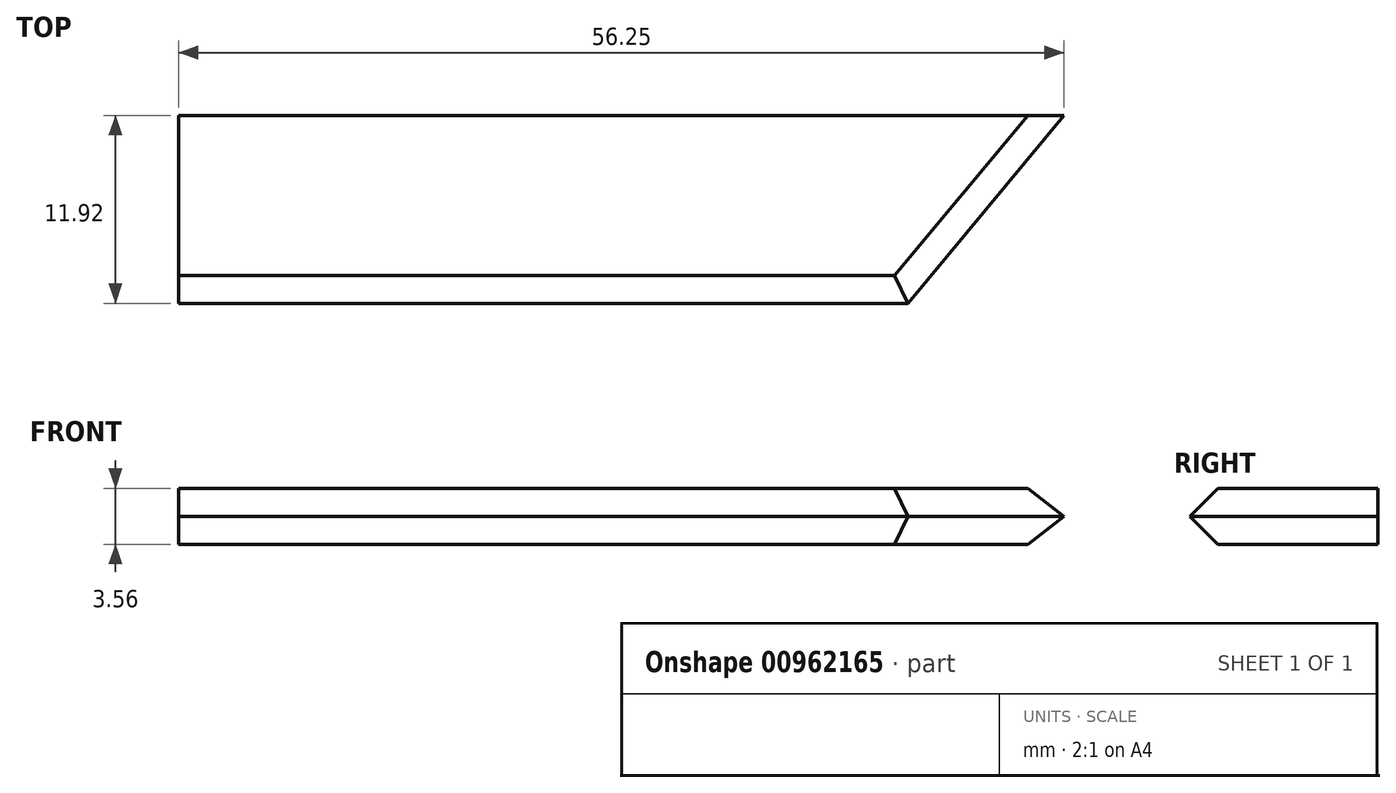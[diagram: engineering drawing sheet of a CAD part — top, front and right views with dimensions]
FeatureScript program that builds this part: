
annotation { "Feature Type Name" : "Feature", "Feature Type Description" : "" }
export const myFeature = defineFeature(function(context is Context, id is Id, definition is map)
    precondition{}
    {
        {
            var Q0;
            Q0=qCreatedBy(makeId("Top.planeOp"),FACE);
            var sketch = newSketch(context, id + "F0", { "sketchPlane" : qUnion([Q0])});
            skLineSegment(sketch, "E0", {"start": v(-43.05, 0) * mm, "end": v(-43.05, 11.92) * mm});
            skLineSegment(sketch, "E1", {"start": v(-43.05, 11.92) * mm, "end": v(13.2, 11.92) * mm});
            skLineSegment(sketch, "E2", {"start": v(13.2, 11.92) * mm, "end": v(3.27, 0) * mm});
            skLineSegment(sketch, "E3", {"start": v(3.27, 0) * mm, "end": v(-43.05, 0) * mm});
            skSolve(sketch);
        }
        {
            var Q0;
            Q0=makeQuery(id+"F0.imprint","IMPRINT",FACE,{"disambiguationData":[TD([[makeQuery(id+"F0.imprint","IMPRINT",EDGE,{"derivedFrom":sQuery(id+"F0.wireOp",EDGE,"E0")}),-1.0]])]});
            extrude(context, id + "F1", {"entities" : qUnion([Q0]), "depth" : 3.56 * mm, "offsetDistance" : 25.4 * mm});
        }
        {
            var Q0;
            Q0=makeQuery(id+"F1.opExtrude","CAP_EDGE",EDGE,{"disambiguationData":[OSD([sQuery(id+"F0.wireOp",EDGE,"E2")])],"isStart":true});
            var Q1;
            Q1=makeQuery(id+"F1.opExtrude","CAP_EDGE",EDGE,{"disambiguationData":[OSD([sQuery(id+"F0.wireOp",EDGE,"E2")])],"isStart":false});
            var Q2;
            Q2=makeQuery(id+"F1.opExtrude","CAP_EDGE",EDGE,{"disambiguationData":[OSD([sQuery(id+"F0.wireOp",EDGE,"E3")])],"isStart":true});
            var Q3;
            Q3=makeQuery(id+"F1.opExtrude","CAP_EDGE",EDGE,{"disambiguationData":[OSD([sQuery(id+"F0.wireOp",EDGE,"E3")])],"isStart":false});
            chamfer(context, id + "F2", {"entities" : qUnion([Q0, Q1, Q2, Q3]), "width" : 1.78 * mm, "tangentPropagation" : true});
        }
    });
